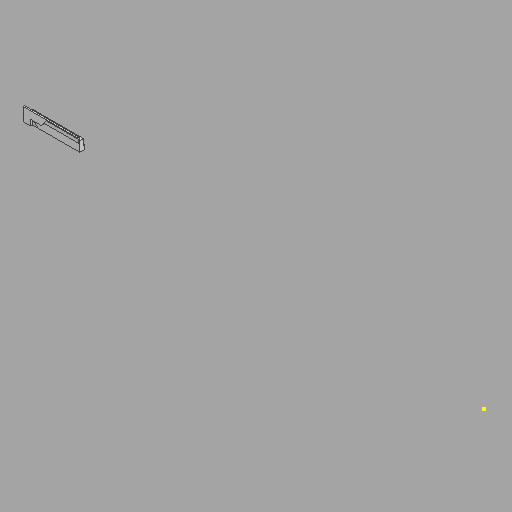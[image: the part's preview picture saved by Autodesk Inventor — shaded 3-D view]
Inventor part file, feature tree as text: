
AUTODESK INVENTOR PART (.ipt)
format: ipt  version: 2023 (Build 270158030, 158C)  size: 310,272 bytes
history: native  units: in
note: dims shown in document units (in); Inventor stores cm internally (conversion verified against a paired STEP export)
features: sketch x2, extrude x1, other x1
ambient origin geometry x8: Origin, YZ Plane, XZ Plane, XY Plane, X Axis, Y Axis, Z Axis, Center Point
bodies: Solid1 (feature_tree)
feature tree (4):
  sketch  "Sketch1"  dims[d0=1.0in d1=0.0in]
  extrude  "Extrusion1"  [1 undecoded]
  sketch  "Sketch2"
  other  "Screen sill I - 1"
note: 1 required parameter value undecoded (feature->parameter linkage not recoverable at this tier; creation-order binding heuristic only, values carry confidence <= 0.55)
